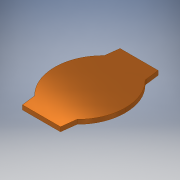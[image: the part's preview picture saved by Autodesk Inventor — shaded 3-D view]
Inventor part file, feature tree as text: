
AUTODESK INVENTOR PART (.ipt)
format: ipt  version: 2019 (Build 230136000, 136)  size: 162,816 bytes
history: native  units: mm
features: other x4, direct_edit x1, extrude x1, sketch x1, projected_geometry x1
ambient origin geometry x8: Origin, YZ Plane, XZ Plane, XY Plane, X Axis, Y Axis, Z Axis, Center Point
bodies: Volumenkörper1 (feature_tree)
feature tree (8):
  other  "Main_afterRhino.ipt"
  direct_edit  "Direktbearbeitung1"
  extrude  "Extrusion1"  Depth=10.769231mm
  other  "Volumenkörper3::Main_afterRhino.ipt"
  other  "Bezeichnung1"
  sketch  "Skizze1"  dims[d0=10.0mm d1=10.769231mm d2=10.0mm d3=10.0mm d4=0.462mm d5=0.0mm]
  projected_geometry  "Projizierte Kontur1"
  other  "Skalierung1"
